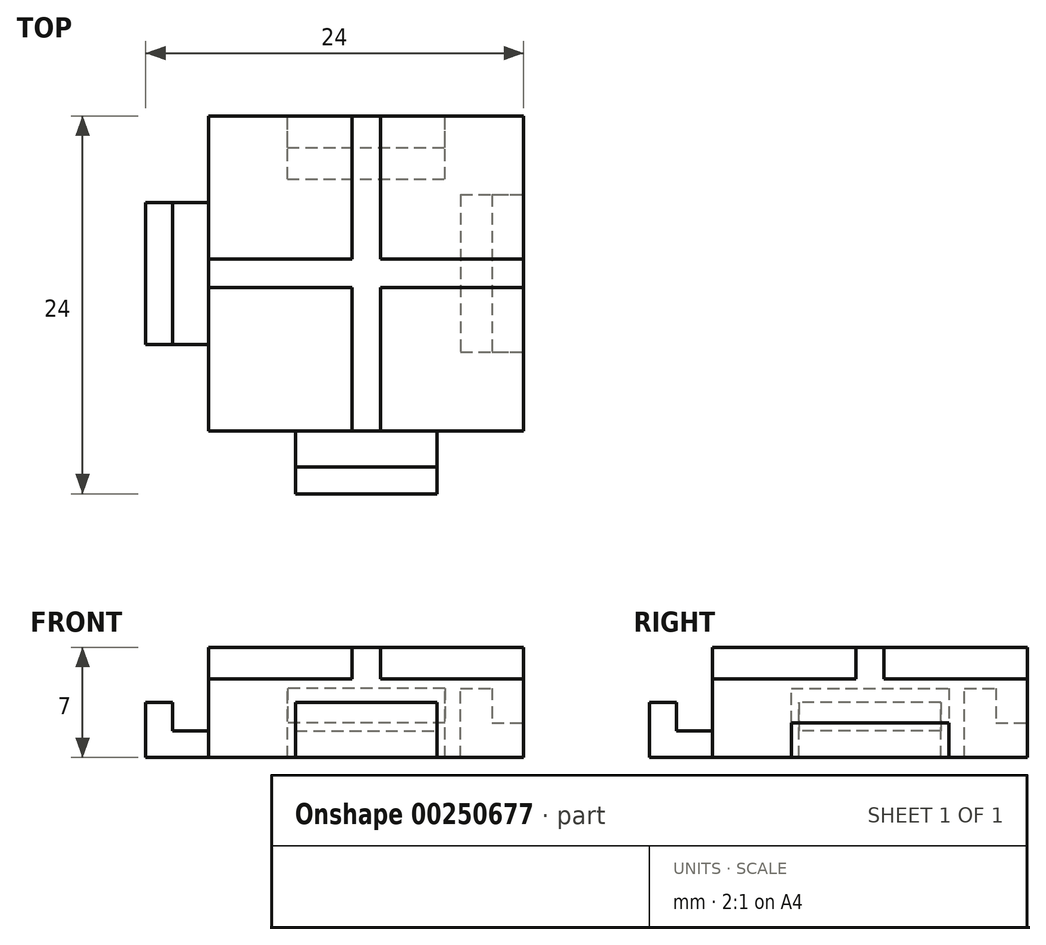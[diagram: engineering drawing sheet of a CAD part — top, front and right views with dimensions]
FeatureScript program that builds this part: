
annotation { "Feature Type Name" : "Feature", "Feature Type Description" : "" }
export const myFeature = defineFeature(function(context is Context, id is Id, definition is map)
    precondition{}
    {
        {
            var Q0;
            Q0=qCreatedBy(makeId("Top.planeOp"),FACE);
            var sketch = newSketch(context, id + "F0", { "sketchPlane" : qUnion([Q0])});
            skLineSegment(sketch, "E0.bottom", {"start": v(-25.78, 21.9) * mm, "end": v(-5.78, 21.9) * mm});
            skLineSegment(sketch, "E0.top", {"start": v(-25.78, 1.9) * mm, "end": v(-5.78, 1.9) * mm});
            skLineSegment(sketch, "E0.left", {"start": v(-25.78, 21.9) * mm, "end": v(-25.78, 1.9) * mm});
            skLineSegment(sketch, "E0.right", {"start": v(-5.78, 21.9) * mm, "end": v(-5.78, 1.9) * mm});
            skSolve(sketch);
        }
        {
            var Q0;
            Q0 = qSketchRegion(id + "F0", true);
            extrude(context, id + "F1", {"entities" : qUnion([Q0]), "depth" : 5 * mm});
        }
        {
            var Q0;
            Q0=makeQuery(id+"F1.opExtrude","CAP_FACE",FACE,{"disambiguationData":[OSD([sQuery(id+"F0.wireOp",EDGE,"E0.bottom"),sQuery(id+"F0.wireOp",EDGE,"E0.top"),sQuery(id+"F0.wireOp",EDGE,"E0.left"),sQuery(id+"F0.wireOp",EDGE,"E0.right")])],"isStart":false});
            var sketch = newSketch(context, id + "F2", { "sketchPlane" : qUnion([Q0])});
            skPoint(sketch, "E1", {"position": v(-15.78, 21.9) * mm});
            skPoint(sketch, "E2", {"position": v(-15.78, 1.9) * mm});
            skPoint(sketch, "E3", {"position": v(-5.78, 11.9) * mm});
            skPoint(sketch, "E4", {"position": v(-25.78, 11.9) * mm});
            skLineSegment(sketch, "E5.bottom", {"start": v(-16.68, 21.9) * mm, "end": v(-14.88, 21.9) * mm});
            skLineSegment(sketch, "E5.top", {"start": v(-16.68, 1.9) * mm, "end": v(-14.88, 1.9) * mm});
            skLineSegment(sketch, "E5.left", {"start": v(-16.68, 21.9) * mm, "end": v(-16.68, 1.9) * mm});
            skLineSegment(sketch, "E5.right", {"start": v(-14.88, 21.9) * mm, "end": v(-14.88, 1.9) * mm});
            skLineSegment(sketch, "E6.bottom", {"start": v(-25.78, 12.8) * mm, "end": v(-5.78, 12.8) * mm});
            skLineSegment(sketch, "E6.top", {"start": v(-25.78, 11) * mm, "end": v(-5.78, 11) * mm});
            skLineSegment(sketch, "E6.left", {"start": v(-25.78, 12.8) * mm, "end": v(-25.78, 11) * mm});
            skLineSegment(sketch, "E6.right", {"start": v(-5.78, 12.8) * mm, "end": v(-5.78, 11) * mm});
            skSolve(sketch);
        }
        {
            var Q0;
            Q0 = qSketchRegion(id + "F2", true);
            extrude(context, id + "F3", {"entities" : qUnion([Q0]), "operationType" : NewBodyOperationType.ADD, "depth" : 2 * mm});
        }
        {
            var Q0;
            Q0=makeQuery(id+"F3.boolean.opBoolean","MERGE",FACE,{"derivedFrom":[makeQuery(id+"F1.opExtrude","SWEPT_FACE",FACE,{"disambiguationData":[OSD([sQuery(id+"F0.wireOp",EDGE,"E0.top")])]}),makeQuery(id+"F3.opExtrude","SWEPT_FACE",FACE,{"disambiguationData":[OSD([sQuery(id+"F2.wireOp",EDGE,"E5.top")])]})]});
            var sketch = newSketch(context, id + "F4", { "sketchPlane" : qUnion([Q0])});
            skLineSegment(sketch, "E7.bottom", {"start": v(-20.28, 0) * mm, "end": v(-11.28, 0) * mm});
            skLineSegment(sketch, "E7.top", {"start": v(-20.28, 1.7) * mm, "end": v(-11.28, 1.7) * mm});
            skLineSegment(sketch, "E7.left", {"start": v(-20.28, 0) * mm, "end": v(-20.28, 1.7) * mm});
            skLineSegment(sketch, "E7.right", {"start": v(-11.28, 0) * mm, "end": v(-11.28, 1.7) * mm});
            skSolve(sketch);
        }
        {
            var Q0;
            Q0 = qSketchRegion(id + "F4", true);
            extrude(context, id + "F5", {"entities" : qUnion([Q0]), "operationType" : NewBodyOperationType.ADD, "depth" : 4 * mm});
        }
        {
            var Q0;
            Q0=makeQuery(id+"F3.boolean.opBoolean","MERGE",FACE,{"derivedFrom":[makeQuery(id+"F1.opExtrude","SWEPT_FACE",FACE,{"disambiguationData":[OSD([sQuery(id+"F0.wireOp",EDGE,"E0.left")])]}),makeQuery(id+"F3.opExtrude","SWEPT_FACE",FACE,{"disambiguationData":[OSD([sQuery(id+"F2.wireOp",EDGE,"E6.left")])]})]});
            var sketch = newSketch(context, id + "F6", { "sketchPlane" : qUnion([Q0])});
            skLineSegment(sketch, "E8.bottom", {"start": v(-16.4, 0) * mm, "end": v(-7.4, 0) * mm});
            skLineSegment(sketch, "E8.top", {"start": v(-16.4, 1.7) * mm, "end": v(-7.4, 1.7) * mm});
            skLineSegment(sketch, "E8.left", {"start": v(-16.4, 0) * mm, "end": v(-16.4, 1.7) * mm});
            skLineSegment(sketch, "E8.right", {"start": v(-7.4, 0) * mm, "end": v(-7.4, 1.7) * mm});
            skSolve(sketch);
        }
        {
            var Q0;
            Q0 = qSketchRegion(id + "F6", true);
            extrude(context, id + "F7", {"entities" : qUnion([Q0]), "operationType" : NewBodyOperationType.ADD, "depth" : 4 * mm});
        }
        {
            var Q0;
            Q0=makeQuery(id+"F3.boolean.opBoolean","MERGE",FACE,{"derivedFrom":[makeQuery(id+"F1.opExtrude","SWEPT_FACE",FACE,{"disambiguationData":[OSD([sQuery(id+"F0.wireOp",EDGE,"E0.bottom")])]}),makeQuery(id+"F3.opExtrude","SWEPT_FACE",FACE,{"disambiguationData":[OSD([sQuery(id+"F2.wireOp",EDGE,"E5.bottom")])]})]});
            var sketch = newSketch(context, id + "F8", { "sketchPlane" : qUnion([Q0])});
            skLineSegment(sketch, "E9.bottom", {"start": v(10.78, 0) * mm, "end": v(20.78, 0) * mm});
            skLineSegment(sketch, "E9.top", {"start": v(10.78, 2.2) * mm, "end": v(20.78, 2.2) * mm});
            skLineSegment(sketch, "E9.left", {"start": v(10.78, 0) * mm, "end": v(10.78, 2.2) * mm});
            skLineSegment(sketch, "E9.right", {"start": v(20.78, 0) * mm, "end": v(20.78, 2.2) * mm});
            skSolve(sketch);
        }
        {
            var Q0;
            Q0 = qSketchRegion(id + "F8", true);
            extrude(context, id + "F9", {"entities" : qUnion([Q0]), "operationType" : NewBodyOperationType.REMOVE, "oppositeDirection" : true, "depth" : 4 * mm});
        }
        {
            var Q0;
            Q0=makeQuery(id+"F3.boolean.opBoolean","MERGE",FACE,{"derivedFrom":[makeQuery(id+"F1.opExtrude","SWEPT_FACE",FACE,{"disambiguationData":[OSD([sQuery(id+"F0.wireOp",EDGE,"E0.right")])]}),makeQuery(id+"F3.opExtrude","SWEPT_FACE",FACE,{"disambiguationData":[OSD([sQuery(id+"F2.wireOp",EDGE,"E6.right")])]})]});
            var sketch = newSketch(context, id + "F10", { "sketchPlane" : qUnion([Q0])});
            skLineSegment(sketch, "E10.bottom", {"start": v(6.9, 0) * mm, "end": v(16.9, 0) * mm});
            skLineSegment(sketch, "E10.top", {"start": v(6.9, 2.2) * mm, "end": v(16.9, 2.2) * mm});
            skLineSegment(sketch, "E10.left", {"start": v(6.9, 0) * mm, "end": v(6.9, 2.2) * mm});
            skLineSegment(sketch, "E10.right", {"start": v(16.9, 0) * mm, "end": v(16.9, 2.2) * mm});
            skSolve(sketch);
        }
        {
            var Q0;
            Q0 = qSketchRegion(id + "F10", true);
            extrude(context, id + "F11", {"entities" : qUnion([Q0]), "operationType" : NewBodyOperationType.REMOVE, "oppositeDirection" : true, "depth" : 4 * mm});
        }
        {
            var Q0;
            Q0=makeQuery(id+"F11.boolean.opBoolean","COPY",FACE,{"derivedFrom":makeQuery(id+"F11.opExtrude","SWEPT_FACE",FACE,{"disambiguationData":[OSD([sQuery(id+"F10.wireOp",EDGE,"E10.top")])]})});
            var sketch = newSketch(context, id + "F12", { "sketchPlane" : qUnion([Q0])});
            skLineSegment(sketch, "E11.bottom", {"start": v(-9.78, -16.9) * mm, "end": v(-7.78, -16.9) * mm});
            skLineSegment(sketch, "E11.top", {"start": v(-9.78, -6.9) * mm, "end": v(-7.78, -6.9) * mm});
            skLineSegment(sketch, "E11.left", {"start": v(-9.78, -16.9) * mm, "end": v(-9.78, -6.9) * mm});
            skLineSegment(sketch, "E11.right", {"start": v(-7.78, -16.9) * mm, "end": v(-7.78, -6.9) * mm});
            skSolve(sketch);
        }
        {
            var Q0;
            Q0 = qSketchRegion(id + "F12", true);
            extrude(context, id + "F13", {"entities" : qUnion([Q0]), "operationType" : NewBodyOperationType.REMOVE, "oppositeDirection" : true, "depth" : 2.2 * mm});
        }
        {
            var Q0;
            Q0=makeQuery(id+"F9.boolean.opBoolean","COPY",FACE,{"derivedFrom":makeQuery(id+"F9.opExtrude","SWEPT_FACE",FACE,{"disambiguationData":[OSD([sQuery(id+"F8.wireOp",EDGE,"E9.top")])]})});
            var sketch = newSketch(context, id + "F14", { "sketchPlane" : qUnion([Q0])});
            skLineSegment(sketch, "E12.bottom", {"start": v(-20.78, -17.9) * mm, "end": v(-10.78, -17.9) * mm});
            skLineSegment(sketch, "E12.top", {"start": v(-20.78, -19.9) * mm, "end": v(-10.78, -19.9) * mm});
            skLineSegment(sketch, "E12.left", {"start": v(-20.78, -17.9) * mm, "end": v(-20.78, -19.9) * mm});
            skLineSegment(sketch, "E12.right", {"start": v(-10.78, -17.9) * mm, "end": v(-10.78, -19.9) * mm});
            skSolve(sketch);
        }
        {
            var Q0;
            Q0 = qSketchRegion(id + "F14", true);
            extrude(context, id + "F15", {"entities" : qUnion([Q0]), "operationType" : NewBodyOperationType.REMOVE, "oppositeDirection" : true, "depth" : 2.2 * mm});
        }
        {
            var Q0;
            Q0=makeQuery(id+"F5.opExtrude","SWEPT_FACE",FACE,{"disambiguationData":[OSD([sQuery(id+"F4.wireOp",EDGE,"E7.top")])]});
            var sketch = newSketch(context, id + "F16", { "sketchPlane" : qUnion([Q0])});
            skLineSegment(sketch, "E13.bottom", {"start": v(-20.28, -2.1) * mm, "end": v(-11.28, -2.1) * mm});
            skLineSegment(sketch, "E13.top", {"start": v(-20.28, -0.4) * mm, "end": v(-11.28, -0.4) * mm});
            skLineSegment(sketch, "E13.left", {"start": v(-20.28, -2.1) * mm, "end": v(-20.28, -0.4) * mm});
            skLineSegment(sketch, "E13.right", {"start": v(-11.28, -2.1) * mm, "end": v(-11.28, -0.4) * mm});
            skSolve(sketch);
        }
        {
            var Q0;
            Q0 = qSketchRegion(id + "F16", true);
            extrude(context, id + "F17", {"entities" : qUnion([Q0]), "operationType" : NewBodyOperationType.ADD, "depth" : 1.8 * mm});
        }
        {
            var Q0;
            Q0=makeQuery(id+"F7.opExtrude","SWEPT_FACE",FACE,{"disambiguationData":[OSD([sQuery(id+"F6.wireOp",EDGE,"E8.top")])]});
            var sketch = newSketch(context, id + "F18", { "sketchPlane" : qUnion([Q0])});
            skLineSegment(sketch, "E14.bottom", {"start": v(-29.78, 16.4) * mm, "end": v(-28.08, 16.4) * mm});
            skLineSegment(sketch, "E14.top", {"start": v(-29.78, 7.4) * mm, "end": v(-28.08, 7.4) * mm});
            skLineSegment(sketch, "E14.left", {"start": v(-29.78, 16.4) * mm, "end": v(-29.78, 7.4) * mm});
            skLineSegment(sketch, "E14.right", {"start": v(-28.08, 16.4) * mm, "end": v(-28.08, 7.4) * mm});
            skSolve(sketch);
        }
        {
            var Q0;
            Q0 = qSketchRegion(id + "F18", true);
            extrude(context, id + "F19", {"entities" : qUnion([Q0]), "operationType" : NewBodyOperationType.ADD, "depth" : 1.8 * mm});
        }
    });
